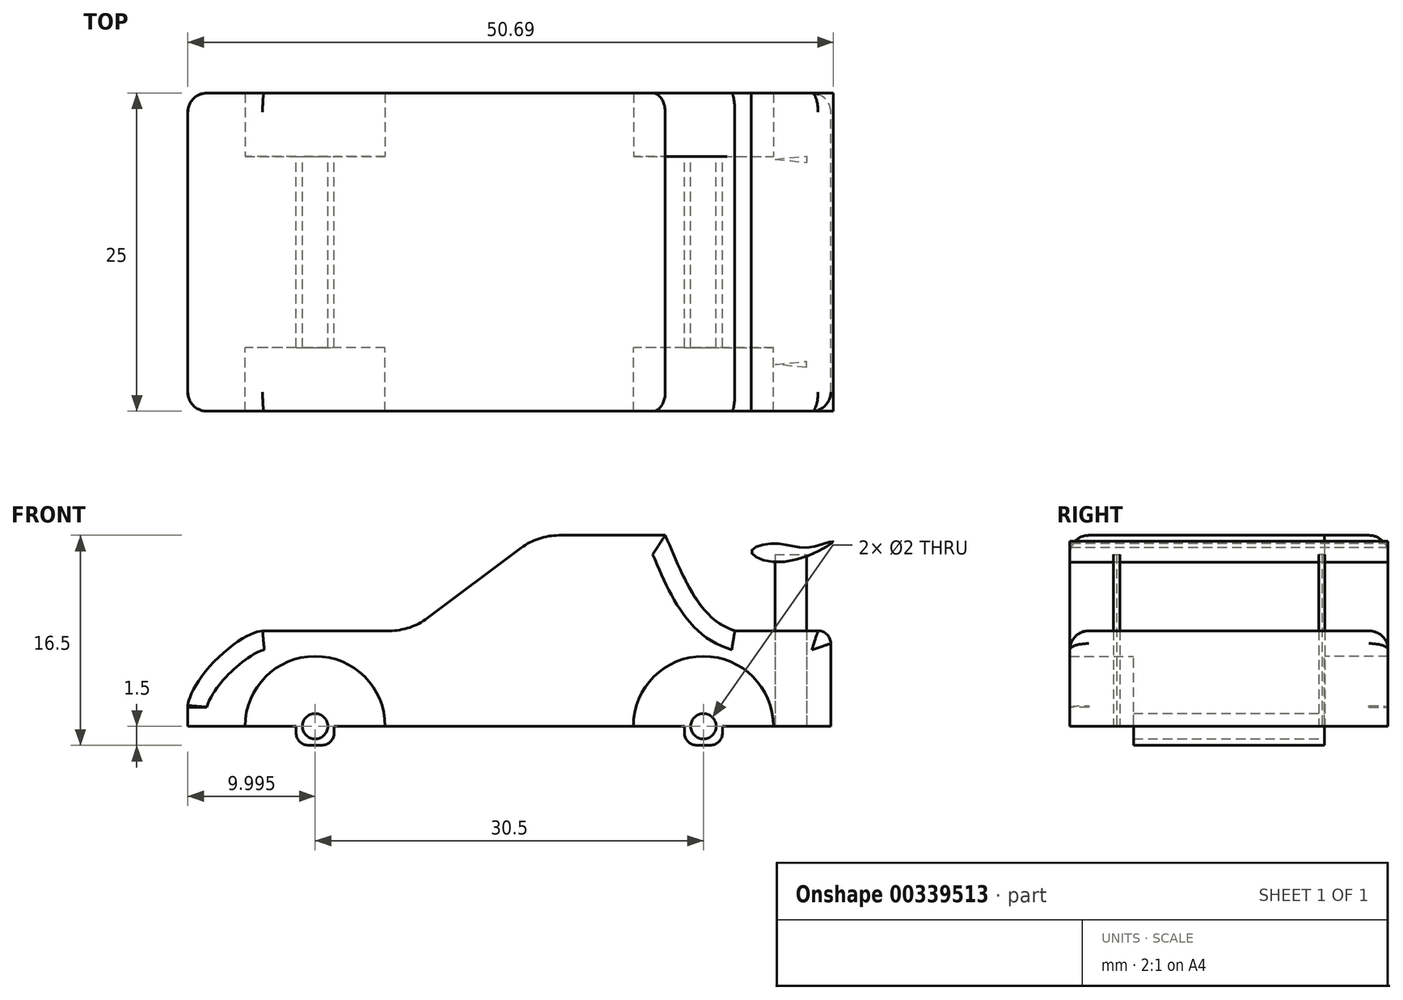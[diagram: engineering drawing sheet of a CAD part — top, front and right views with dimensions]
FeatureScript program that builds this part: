
annotation { "Feature Type Name" : "Feature", "Feature Type Description" : "" }
export const myFeature = defineFeature(function(context is Context, id is Id, definition is map)
    precondition{}
    {
        {
            var Q0;
            Q0=qCreatedBy(makeId("Front.planeOp"),FACE);
            var sketch = newSketch(context, id + "F0", { "sketchPlane" : qUnion([Q0])});
            skLineSegment(sketch, "E0.bottom", {"start": v(-68.5, 0) * mm, "end": v(-48.5, 0) * mm});
            skLineSegment(sketch, "E1.bottom", {"start": v(-68.5, 0) * mm, "end": v(-86, 0) * mm});
            skLineSegment(sketch, "E1.top", {"start": v(-68.5, 7.5) * mm, "end": v(-86, 7.5) * mm});
            skLineSegment(sketch, "E1.left", {"start": v(-68.5, 0) * mm, "end": v(-68.5, 7.5) * mm, "construction": true});
            skLineSegment(sketch, "E1.right", {"start": v(-86, 0) * mm, "end": v(-86, 7.5) * mm});
            skPoint(sketch, "E2.oppositeSnap0", {"position": v(-48.5, 7.5) * mm});
            skLineSegment(sketch, "E2.bottom", {"start": v(-48.5, 0) * mm, "end": v(-35.5, 0) * mm});
            skLineSegment(sketch, "E2.left", {"start": v(-48.5, 0) * mm, "end": v(-48.5, 7.5) * mm, "construction": true});
            skLineSegment(sketch, "E2.right", {"start": v(-35.5, 0) * mm, "end": v(-35.5, 7.5) * mm});
            skLineSegment(sketch, "E3", {"start": v(-48.5, 15) * mm, "end": v(-48.5, 7.5) * mm, "construction": true});
            skFitSpline(sketch, "E4", {"points": [v(-48.5, 15) * mm, v(-45.74, 9.52) * mm, v(-43.04, 7.5) * mm], "startDerivative": vector(3.9, -10.8) * mm, "endDerivative": vector(9.76, -3.83) * mm});
            skLineSegment(sketch, "E5", {"start": v(-35.5, 7.5) * mm, "end": v(-43.04, 7.5) * mm});
            skLineSegment(sketch, "E6", {"start": v(-68.5, 7.5) * mm, "end": v(-58.5, 15) * mm});
            skLineSegment(sketch, "E7", {"start": v(-58.5, 15) * mm, "end": v(-48.5, 15) * mm});
            skLineSegment(sketch, "E8.bottom", {"start": v(-77.5, 0) * mm, "end": v(-74.5, 0) * mm});
            skLineSegment(sketch, "E8.top", {"start": v(-77.5, -1.5) * mm, "end": v(-74.5, -1.5) * mm});
            skLineSegment(sketch, "E8.left", {"start": v(-77.5, 0) * mm, "end": v(-77.5, -1.5) * mm});
            skLineSegment(sketch, "E8.right", {"start": v(-74.5, 0) * mm, "end": v(-74.5, -1.5) * mm});
            skLineSegment(sketch, "E9.bottom", {"start": v(-47, 0) * mm, "end": v(-44, 0) * mm});
            skLineSegment(sketch, "E9.top", {"start": v(-47, -1.5) * mm, "end": v(-44, -1.5) * mm});
            skLineSegment(sketch, "E9.left", {"start": v(-44, 0) * mm, "end": v(-44, -1.5) * mm});
            skLineSegment(sketch, "E9.right", {"start": v(-47, 0) * mm, "end": v(-47, -1.5) * mm});
            skLineSegment(sketch, "E10", {"start": v(-76, -1.5) * mm, "end": v(-76, 0) * mm, "construction": true});
            skLineSegment(sketch, "E11", {"start": v(-45.5, 0) * mm, "end": v(-45.5, -1.5) * mm, "construction": true});
            skCircle(sketch, "E12", {"center": v(-76, 0) * mm, "radius": 1 * mm});
            skCircle(sketch, "E13", {"center": v(-45.5, 0) * mm, "radius": 1 * mm});
            skSolve(sketch);
        }
        {
            var Q0;
            Q0 = qSketchRegion(id + "F0", true);
            extrude(context, id + "F1", {"entities" : qUnion([Q0]), "depth" : 15 * mm, "symmetric" : true});
        }
        {
            var Q0;
            Q0=makeQuery(id+"F1.opExtrude","CAP_FACE",FACE,{"disambiguationData":[OSD([sQuery(id+"F0.wireOp",EDGE,"E0.bottom"),sQuery(id+"F0.wireOp",EDGE,"E1.bottom"),sQuery(id+"F0.wireOp",EDGE,"E1.top"),sQuery(id+"F0.wireOp",EDGE,"E1.right"),sQuery(id+"F0.wireOp",EDGE,"E2.bottom"),sQuery(id+"F0.wireOp",EDGE,"E2.right"),sQuery(id+"F0.wireOp",EDGE,"E4"),sQuery(id+"F0.wireOp",EDGE,"E5"),sQuery(id+"F0.wireOp",EDGE,"E6"),sQuery(id+"F0.wireOp",EDGE,"E7")])],"isStart":true});
            var sketch = newSketch(context, id + "F2", { "sketchPlane" : qUnion([Q0])});
            skLineSegment(sketch, "E14", {"start": v(35.5, 0) * mm, "end": v(40, 0) * mm});
            skLineSegment(sketch, "E15", {"start": v(86, 0) * mm, "end": v(86, 7.5) * mm});
            skLineSegment(sketch, "E16", {"start": v(86, 7.5) * mm, "end": v(68.5, 7.5) * mm});
            skLineSegment(sketch, "E17", {"start": v(68.5, 7.5) * mm, "end": v(58.5, 15) * mm});
            skLineSegment(sketch, "E18", {"start": v(58.5, 15) * mm, "end": v(48.5, 15) * mm});
            skLineSegment(sketch, "E19", {"start": v(43.04, 7.5) * mm, "end": v(35.5, 7.5) * mm});
            skLineSegment(sketch, "E20", {"start": v(35.5, 7.5) * mm, "end": v(35.5, 0) * mm});
            skFitSpline(sketch, "E21", {"points": [v(48.5, 15) * mm, v(46.48, 10.66) * mm, v(43.04, 7.5) * mm], "startDerivative": vector(-3.32, -8.42) * mm, "endDerivative": vector(-11.77, -4.47) * mm});
            skLineSegment(sketch, "E22", {"start": v(51, 0) * mm, "end": v(70.5, 0) * mm});
            skLineSegment(sketch, "E23", {"start": v(40, 0) * mm, "end": v(51, 0) * mm, "construction": true});
            skLineSegment(sketch, "E24", {"start": v(70.5, 0) * mm, "end": v(81.5, 0) * mm, "construction": true});
            skLineSegment(sketch, "E25", {"start": v(81.5, 0) * mm, "end": v(86, 0) * mm});
            skArc(sketch, "E26", {"start": v(40, 0) * mm, "mid": v(45.5, -5.5) * mm, "end": v(51, 0) * mm, "construction": true});
            skArc(sketch, "E27", {"start": v(51, 0) * mm, "mid": v(45.5, 5.5) * mm, "end": v(40, 0) * mm});
            skArc(sketch, "E28", {"start": v(70.5, 0) * mm, "mid": v(76, -5.5) * mm, "end": v(81.5, 0) * mm, "construction": true});
            skArc(sketch, "E29", {"start": v(81.5, 0) * mm, "mid": v(76, 5.5) * mm, "end": v(70.5, 0) * mm});
            skSolve(sketch);
        }
        {
            var Q0;
            Q0 = qSketchRegion(id + "F2", true);
            extrude(context, id + "F3", {"entities" : qUnion([Q0]), "operationType" : NewBodyOperationType.ADD, "depth" : 5 * mm});
        }
        {
            var Q0;
            Q0=makeQuery(id+"F1.opExtrude","CAP_FACE",FACE,{"disambiguationData":[OSD([sQuery(id+"F0.wireOp",EDGE,"E0.bottom"),sQuery(id+"F0.wireOp",EDGE,"E1.bottom"),sQuery(id+"F0.wireOp",EDGE,"E1.top"),sQuery(id+"F0.wireOp",EDGE,"E1.right"),sQuery(id+"F0.wireOp",EDGE,"E2.bottom"),sQuery(id+"F0.wireOp",EDGE,"E2.right"),sQuery(id+"F0.wireOp",EDGE,"E4"),sQuery(id+"F0.wireOp",EDGE,"E5"),sQuery(id+"F0.wireOp",EDGE,"E6"),sQuery(id+"F0.wireOp",EDGE,"E7")])],"isStart":false});
            var sketch = newSketch(context, id + "F4", { "sketchPlane" : qUnion([Q0])});
            skLineSegment(sketch, "E30", {"start": v(-86, 0) * mm, "end": v(-81.5, 0) * mm});
            skLineSegment(sketch, "E31", {"start": v(-35.5, 0) * mm, "end": v(-35.5, 7.5) * mm});
            skLineSegment(sketch, "E32", {"start": v(-35.5, 7.5) * mm, "end": v(-43.04, 7.5) * mm});
            skLineSegment(sketch, "E33", {"start": v(-48.5, 15) * mm, "end": v(-58.5, 15) * mm});
            skLineSegment(sketch, "E34", {"start": v(-58.5, 15) * mm, "end": v(-68.5, 7.5) * mm});
            skLineSegment(sketch, "E35", {"start": v(-68.5, 7.5) * mm, "end": v(-86, 7.5) * mm});
            skLineSegment(sketch, "E36", {"start": v(-86, 7.5) * mm, "end": v(-86, 0) * mm});
            skFitSpline(sketch, "E37", {"points": [v(-48.5, 15) * mm, v(-46.48, 10.66) * mm, v(-43.04, 7.5) * mm], "startDerivative": vector(7.58, -17.62) * mm, "endDerivative": vector(11.63, -3.86) * mm});
            skArc(sketch, "E38", {"start": v(-81.5, 0) * mm, "mid": v(-76, -5.5) * mm, "end": v(-70.5, 0) * mm, "construction": true});
            skArc(sketch, "E39", {"start": v(-70.5, 0) * mm, "mid": v(-76, 5.5) * mm, "end": v(-81.5, 0) * mm});
            skArc(sketch, "E40", {"start": v(-51, 0) * mm, "mid": v(-45.5, -5.5) * mm, "end": v(-40, 0) * mm, "construction": true});
            skArc(sketch, "E41", {"start": v(-40, 0) * mm, "mid": v(-45.5, 5.5) * mm, "end": v(-51, 0) * mm});
            skLineSegment(sketch, "E42", {"start": v(-81.5, 0) * mm, "end": v(-70.5, 0) * mm, "construction": true});
            skLineSegment(sketch, "E43", {"start": v(-70.5, 0) * mm, "end": v(-51, 0) * mm});
            skLineSegment(sketch, "E44", {"start": v(-51, 0) * mm, "end": v(-40, 0) * mm, "construction": true});
            skLineSegment(sketch, "E45", {"start": v(-40, 0) * mm, "end": v(-35.5, 0) * mm});
            skSolve(sketch);
        }
        {
            var Q0;
            Q0 = qSketchRegion(id + "F4", true);
            extrude(context, id + "F5", {"entities" : qUnion([Q0]), "operationType" : NewBodyOperationType.ADD, "depth" : 5 * mm});
        }
        {
            var Q0;
            Q0=makeQuery(id+"F5.boolean.opBoolean","MERGE",EDGE,{"derivedFrom":[makeQuery(id+"F3.boolean.opBoolean","MERGE",EDGE,{"derivedFrom":[makeQuery(id+"F1.opExtrude","SWEPT_EDGE",EDGE,{"disambiguationData":[OSD([sQuery(id+"F0.wireOp",EDGE,"E1.top"),sQuery(id+"F0.wireOp",EDGE,"E6")])]}),makeQuery(id+"F3.opExtrude","SWEPT_EDGE",EDGE,{"disambiguationData":[OSD([sQuery(id+"F2.wireOp",EDGE,"E16"),sQuery(id+"F2.wireOp",EDGE,"E17")])]})]}),makeQuery(id+"F5.opExtrude","SWEPT_EDGE",EDGE,{"disambiguationData":[OSD([sQuery(id+"F4.wireOp",EDGE,"E34"),sQuery(id+"F4.wireOp",EDGE,"E35")])]})]});
            fillet(context, id + "F6", {"entities" : qUnion([Q0]), "radius" : 5 * mm, "tangentPropagation" : true, "allowEdgeOverflow" : false});
        }
        {
            var Q0;
            Q0=makeQuery(id+"F5.boolean.opBoolean","MERGE",EDGE,{"derivedFrom":[makeQuery(id+"F3.boolean.opBoolean","MERGE",EDGE,{"derivedFrom":[makeQuery(id+"F1.opExtrude","SWEPT_EDGE",EDGE,{"disambiguationData":[OSD([sQuery(id+"F0.wireOp",EDGE,"E6"),sQuery(id+"F0.wireOp",EDGE,"E7")])]}),makeQuery(id+"F3.opExtrude","SWEPT_EDGE",EDGE,{"disambiguationData":[OSD([sQuery(id+"F2.wireOp",EDGE,"E17"),sQuery(id+"F2.wireOp",EDGE,"E18")])]})]}),makeQuery(id+"F5.opExtrude","SWEPT_EDGE",EDGE,{"disambiguationData":[OSD([sQuery(id+"F4.wireOp",EDGE,"E33"),sQuery(id+"F4.wireOp",EDGE,"E34")])]})]});
            fillet(context, id + "F7", {"entities" : qUnion([Q0]), "radius" : 5 * mm, "tangentPropagation" : true, "allowEdgeOverflow" : false});
        }
        {
            var Q0;
            Q0=makeQuery(id+"F1.opExtrude","SWEPT_EDGE",EDGE,{"disambiguationData":[OSD([sQuery(id+"F0.wireOp",EDGE,"E8.top"),sQuery(id+"F0.wireOp",EDGE,"E8.left")])]});
            fillet(context, id + "F8", {"entities" : qUnion([Q0]), "radius" : 1 * mm, "tangentPropagation" : true, "allowEdgeOverflow" : false});
        }
        {
            var Q0;
            Q0=makeQuery(id+"F1.opExtrude","SWEPT_EDGE",EDGE,{"disambiguationData":[OSD([sQuery(id+"F0.wireOp",EDGE,"E8.top"),sQuery(id+"F0.wireOp",EDGE,"E8.right")])]});
            var Q1;
            Q1=makeQuery(id+"F1.opExtrude","SWEPT_EDGE",EDGE,{"disambiguationData":[OSD([sQuery(id+"F0.wireOp",EDGE,"E9.top"),sQuery(id+"F0.wireOp",EDGE,"E9.left")])]});
            var Q2;
            Q2=makeQuery(id+"F1.opExtrude","SWEPT_EDGE",EDGE,{"disambiguationData":[OSD([sQuery(id+"F0.wireOp",EDGE,"E9.top"),sQuery(id+"F0.wireOp",EDGE,"E9.right")])]});
            fillet(context, id + "F9", {"entities" : qUnion([Q0, Q1, Q2]), "radius" : 1 * mm, "tangentPropagation" : true, "allowEdgeOverflow" : false});
        }
        {
            var Q0;
            Q0=makeQuery(id+"F5.boolean.opBoolean","MERGE",EDGE,{"derivedFrom":[makeQuery(id+"F3.boolean.opBoolean","MERGE",EDGE,{"derivedFrom":[makeQuery(id+"F1.opExtrude","SWEPT_EDGE",EDGE,{"disambiguationData":[OSD([sQuery(id+"F0.wireOp",EDGE,"E1.top"),sQuery(id+"F0.wireOp",EDGE,"E1.right")])]}),makeQuery(id+"F3.opExtrude","SWEPT_EDGE",EDGE,{"disambiguationData":[OSD([sQuery(id+"F2.wireOp",EDGE,"E15"),sQuery(id+"F2.wireOp",EDGE,"E16")])]})]}),makeQuery(id+"F5.opExtrude","SWEPT_EDGE",EDGE,{"disambiguationData":[OSD([sQuery(id+"F4.wireOp",EDGE,"E35"),sQuery(id+"F4.wireOp",EDGE,"E36")])]})]});
            fillet(context, id + "F10", {"entities" : qUnion([Q0]), "radius" : 6 * mm, "tangentPropagation" : true, "rho" : 0.25, "crossSection" : FilletCrossSection.CONIC, "allowEdgeOverflow" : false});
        }
        {
            var Q0;
            Q0=makeQuery(id+"F3.opExtrude","CAP_EDGE",EDGE,{"disambiguationData":[OSD([sQuery(id+"F2.wireOp",EDGE,"E16")])],"isStart":false});
            var Q1;
            Q1=makeQuery(id+"F5.opExtrude","CAP_EDGE",EDGE,{"disambiguationData":[OSD([sQuery(id+"F4.wireOp",EDGE,"E35")])],"isStart":false});
            fillet(context, id + "F11", {"entities" : qUnion([Q0, Q1]), "radius" : 1.5 * mm, "tangentPropagation" : true, "allowEdgeOverflow" : false});
        }
        {
            var Q0;
            Q0=makeQuery(id+"F3.opExtrude","CAP_EDGE",EDGE,{"disambiguationData":[OSD([sQuery(id+"F2.wireOp",EDGE,"E20")])],"isStart":false});
            var Q1;
            Q1=makeQuery(id+"F5.opExtrude","CAP_EDGE",EDGE,{"disambiguationData":[OSD([sQuery(id+"F4.wireOp",EDGE,"E31")])],"isStart":false});
            fillet(context, id + "F12", {"entities" : qUnion([Q0, Q1]), "radius" : 1.5 * mm, "tangentPropagation" : true, "allowEdgeOverflow" : false});
        }
        {
            var Q0;
            Q0=makeQuery(id+"F5.opExtrude","CAP_EDGE",EDGE,{"disambiguationData":[OSD([sQuery(id+"F4.wireOp",EDGE,"E32")])],"isStart":false});
            var Q1;
            Q1=makeQuery(id+"F3.opExtrude","CAP_EDGE",EDGE,{"disambiguationData":[OSD([sQuery(id+"F2.wireOp",EDGE,"E19")])],"isStart":false});
            fillet(context, id + "F13", {"entities" : qUnion([Q0, Q1]), "radius" : 1.5 * mm, "allowEdgeOverflow" : false});
        }
        {
            var Q0;
            Q0=makeQuery(id+"F5.opExtrude","CAP_EDGE",EDGE,{"disambiguationData":[OSD([sQuery(id+"F4.wireOp",EDGE,"E37")])],"isStart":false});
            var Q1;
            Q1=makeQuery(id+"F3.opExtrude","CAP_EDGE",EDGE,{"disambiguationData":[OSD([sQuery(id+"F2.wireOp",EDGE,"E21")])],"isStart":false});
            fillet(context, id + "F14", {"entities" : qUnion([Q0, Q1]), "radius" : 1.5 * mm, "allowEdgeOverflow" : false});
        }
        {
            var Q0;
            Q0=makeQuery(id+"F5.boolean.opBoolean","MERGE",EDGE,{"derivedFrom":[makeQuery(id+"F3.boolean.opBoolean","MERGE",EDGE,{"derivedFrom":[makeQuery(id+"F1.opExtrude","SWEPT_EDGE",EDGE,{"disambiguationData":[OSD([sQuery(id+"F0.wireOp",EDGE,"E2.right"),sQuery(id+"F0.wireOp",EDGE,"E5")])]}),makeQuery(id+"F3.opExtrude","SWEPT_EDGE",EDGE,{"disambiguationData":[OSD([sQuery(id+"F2.wireOp",EDGE,"E19"),sQuery(id+"F2.wireOp",EDGE,"E20")])]})]}),makeQuery(id+"F5.opExtrude","SWEPT_EDGE",EDGE,{"disambiguationData":[OSD([sQuery(id+"F4.wireOp",EDGE,"E31"),sQuery(id+"F4.wireOp",EDGE,"E32")])]})]});
            fillet(context, id + "F15", {"entities" : qUnion([Q0]), "radius" : 1 * mm, "tangentPropagation" : true, "allowEdgeOverflow" : false});
        }
        {
            var Q0;
            Q0=makeQuery(id+"F5.opExtrude","CAP_FACE",FACE,{"disambiguationData":[OSD([sQuery(id+"F4.wireOp",EDGE,"E30"),sQuery(id+"F4.wireOp",EDGE,"E31"),sQuery(id+"F4.wireOp",EDGE,"E32"),sQuery(id+"F4.wireOp",EDGE,"E33"),sQuery(id+"F4.wireOp",EDGE,"E34"),sQuery(id+"F4.wireOp",EDGE,"E35"),sQuery(id+"F4.wireOp",EDGE,"E36"),sQuery(id+"F4.wireOp",EDGE,"E37"),sQuery(id+"F4.wireOp",EDGE,"E39"),sQuery(id+"F4.wireOp",EDGE,"E41"),sQuery(id+"F4.wireOp",EDGE,"E43"),sQuery(id+"F4.wireOp",EDGE,"E45")])],"isStart":false});
            var sketch = newSketch(context, id + "F16", { "sketchPlane" : qUnion([Q0])});
            skFitSpline(sketch, "E46", {"points": [v(-39.15, 12.91) * mm, v(-41.74, 13.77) * mm, v(-39.74, 14.35) * mm, v(-37.3, 14.04) * mm, v(-35.31, 14.51) * mm, v(-39.15, 12.91) * mm]});
            skSolve(sketch);
        }
        {
            var Q0;
            Q0=makeQuery(id+"F16.imprint","IMPRINT",FACE,{"disambiguationData":[TD([[makeQuery(id+"F16.imprint","IMPRINT",EDGE,{"derivedFrom":sQuery(id+"F16.wireOp",EDGE,"E46")}),-1.0]])]});
            extrude(context, id + "F17", {"entities" : qUnion([Q0]), "oppositeDirection" : true, "depth" : 25 * mm});
        }
        {
            var Q0;
            Q0=qCreatedBy(makeId("Top.planeOp"),FACE);
            var sketch = newSketch(context, id + "F18", { "sketchPlane" : qUnion([Q0])});
            skLineSegment(sketch, "E47.right", {"start": v(-37.39, 7.55) * mm, "end": v(-37.39, 7.05) * mm});
            skLineSegment(sketch, "E48.right", {"start": v(-37.39, -9.07) * mm, "end": v(-37.39, -8.57) * mm});
            skLineSegment(sketch, "E49", {"start": v(-37.39, -9.07) * mm, "end": v(-39.89, -8.82) * mm});
            skLineSegment(sketch, "E50", {"start": v(-39.89, -8.82) * mm, "end": v(-37.39, -8.57) * mm});
            skLineSegment(sketch, "E51", {"start": v(-39.89, 7.3) * mm, "end": v(-37.39, 7.55) * mm});
            skLineSegment(sketch, "E52", {"start": v(-39.89, 7.3) * mm, "end": v(-37.39, 7.05) * mm});
            skSolve(sketch);
        }
        {
            var Q0;
            Q0 = qSketchRegion(id + "F18", true);
            extrude(context, id + "F19", {"entities" : qUnion([Q0]), "depth" : 13.5 * mm});
        }
    });
